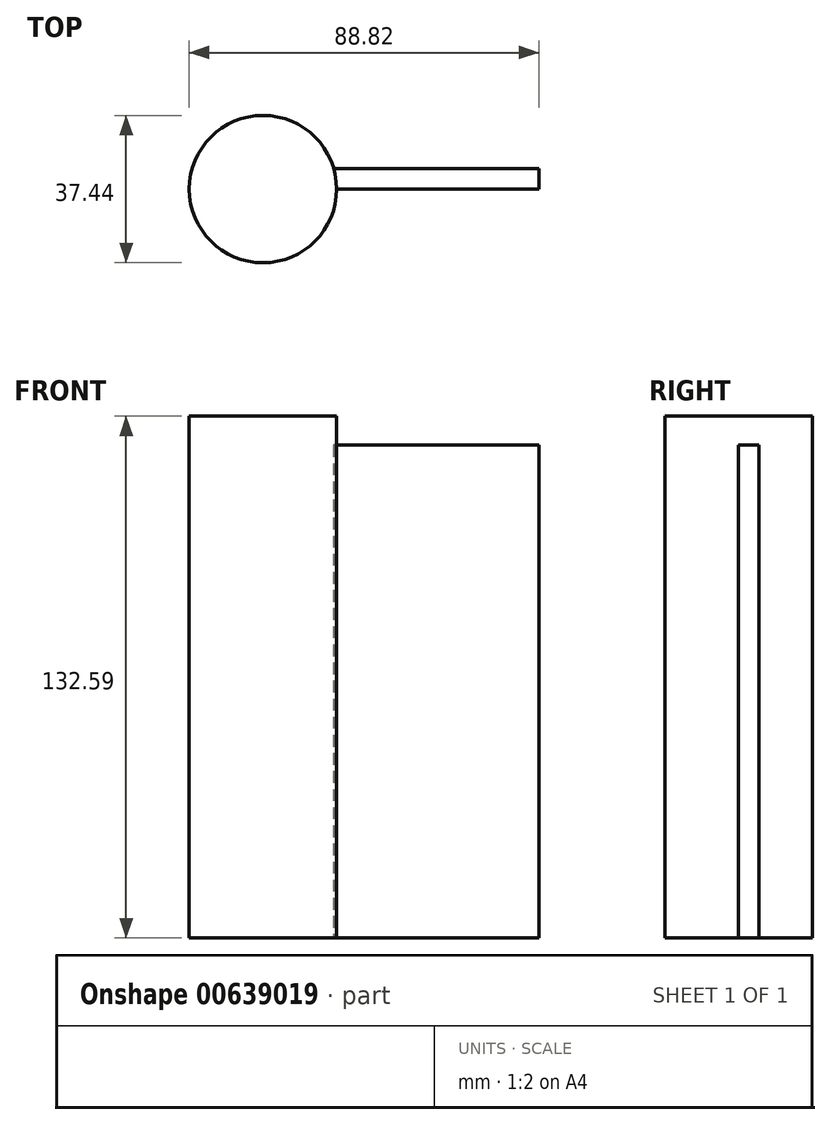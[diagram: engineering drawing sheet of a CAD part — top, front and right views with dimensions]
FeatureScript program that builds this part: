
annotation { "Feature Type Name" : "Feature", "Feature Type Description" : "" }
export const myFeature = defineFeature(function(context is Context, id is Id, definition is map)
    precondition{}
    {
        {
            var Q0;
            Q0=qCreatedBy(makeId("Top.planeOp"),FACE);
            var sketch = newSketch(context, id + "F0", { "sketchPlane" : qUnion([Q0])});
            skCircle(sketch, "E0", {"center": v(0, 0) * mm, "radius": 18.72 * mm});
            skSolve(sketch);
        }
        {
            var Q0;
            Q0 = qSketchRegion(id + "F0", true);
            extrude(context, id + "F1", {"entities" : qUnion([Q0]), "depth" : 132.6 * mm, "offsetDistance" : 25.4 * mm});
        }
        {
            var Q0;
            Q0=qCreatedBy(makeId("Right.planeOp"),FACE);
            var sketch = newSketch(context, id + "F2", { "sketchPlane" : qUnion([Q0])});
            skLineSegment(sketch, "E1.bottom", {"start": v(0, 125.22) * mm, "end": v(5.2, 125.22) * mm});
            skLineSegment(sketch, "E1.top", {"start": v(0, 0) * mm, "end": v(5.2, 0) * mm});
            skLineSegment(sketch, "E1.left", {"start": v(0, 125.22) * mm, "end": v(0, 0) * mm});
            skLineSegment(sketch, "E1.right", {"start": v(5.2, 125.22) * mm, "end": v(5.2, 0) * mm});
            skSolve(sketch);
        }
        {
            var Q0;
            Q0 = qSketchRegion(id + "F2", true);
            extrude(context, id + "F3", {"entities" : qUnion([Q0]), "operationType" : NewBodyOperationType.ADD, "depth" : 70.1 * mm, "offsetDistance" : 25.4 * mm});
        }
    });
